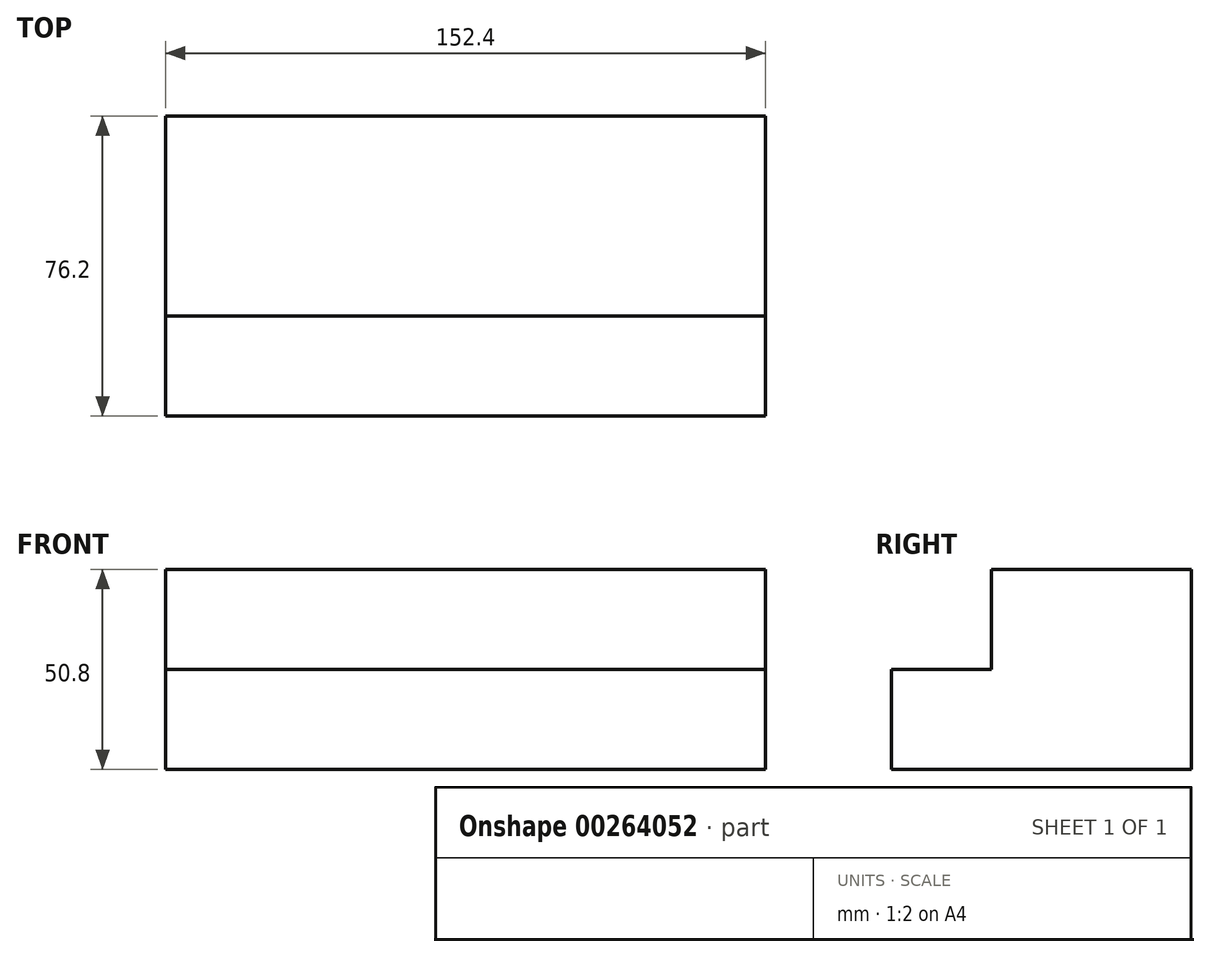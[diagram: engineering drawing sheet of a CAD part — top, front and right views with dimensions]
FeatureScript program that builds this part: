
annotation { "Feature Type Name" : "Feature", "Feature Type Description" : "" }
export const myFeature = defineFeature(function(context is Context, id is Id, definition is map)
    precondition{}
    {
        {
            var Q0;
            Q0=qCreatedBy(makeId("Right.planeOp"),FACE);
            var sketch = newSketch(context, id + "F0", { "sketchPlane" : qUnion([Q0])});
            skLineSegment(sketch, "E0", {"start": v(0, 0) * mm, "end": v(76.2, 0) * mm});
            skLineSegment(sketch, "E1", {"start": v(76.2, 0) * mm, "end": v(76.2, 50.8) * mm});
            skLineSegment(sketch, "E2", {"start": v(76.2, 50.8) * mm, "end": v(25.4, 50.8) * mm});
            skLineSegment(sketch, "E3", {"start": v(25.4, 50.8) * mm, "end": v(25.4, 25.4) * mm});
            skLineSegment(sketch, "E4", {"start": v(25.4, 25.4) * mm, "end": v(0, 25.4) * mm});
            skLineSegment(sketch, "E5", {"start": v(0, 25.4) * mm, "end": v(0, 0) * mm});
            skSolve(sketch);
        }
        {
            var Q0;
            Q0=makeQuery(id+"F0.imprint","IMPRINT",FACE,{"disambiguationData":[TD([[makeQuery(id+"F0.imprint","IMPRINT",EDGE,{"derivedFrom":sQuery(id+"F0.wireOp",EDGE,"E0")}),1.0]])]});
            extrude(context, id + "F1", {"entities" : qUnion([Q0]), "depth" : 152.4 * mm});
        }
    });
